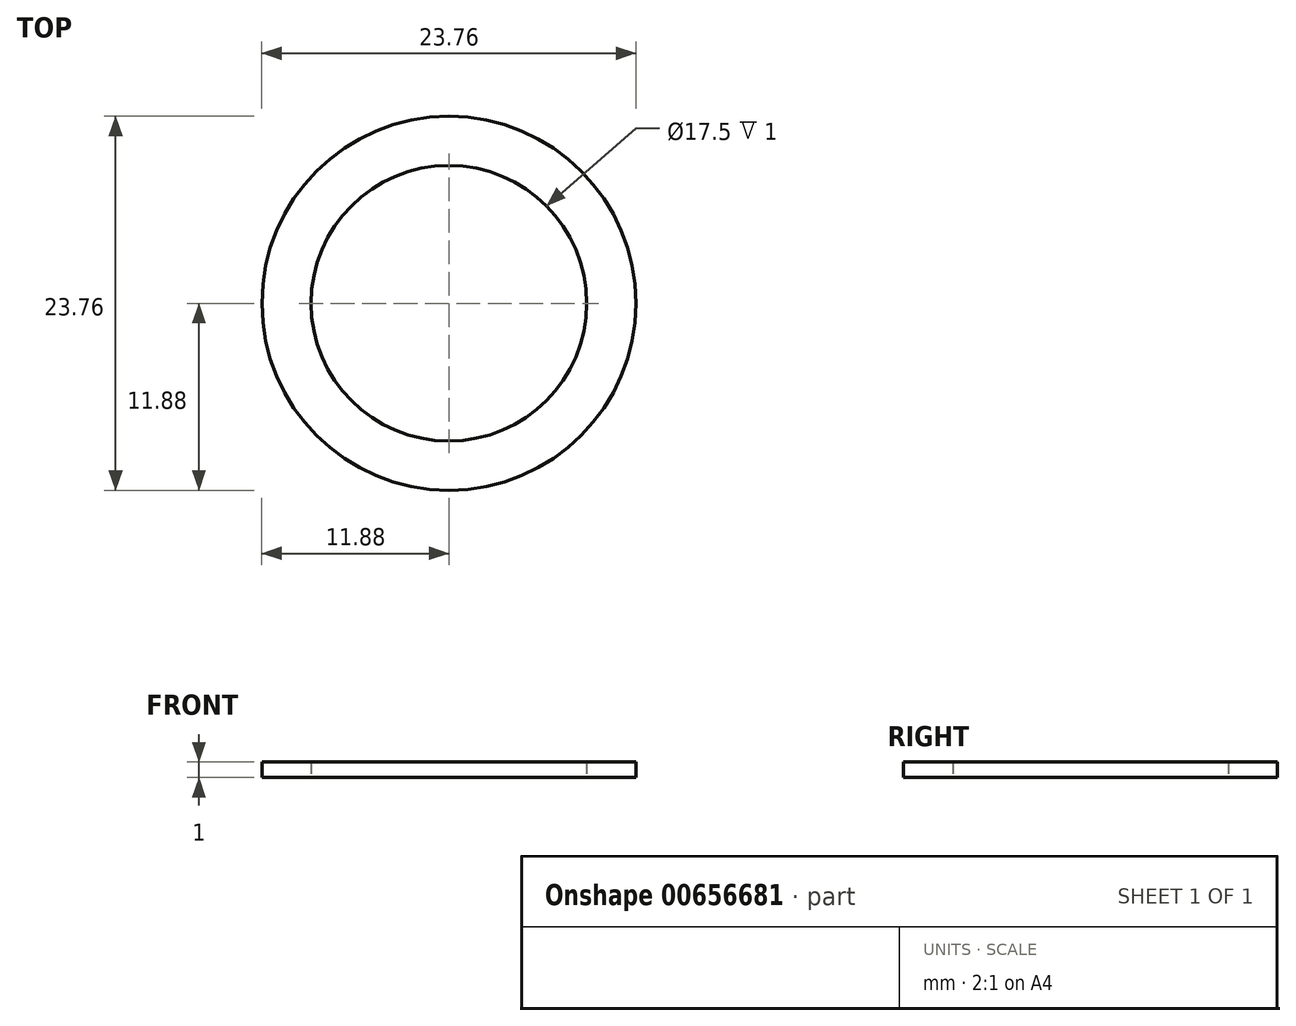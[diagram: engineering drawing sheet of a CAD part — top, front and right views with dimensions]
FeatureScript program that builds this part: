
annotation { "Feature Type Name" : "Feature", "Feature Type Description" : "" }
export const myFeature = defineFeature(function(context is Context, id is Id, definition is map)
    precondition{}
    {
        {
            var Q0;
            Q0=qCreatedBy(makeId("Top.planeOp"),FACE);
            var sketch = newSketch(context, id + "F0", { "sketchPlane" : qUnion([Q0])});
            skCircle(sketch, "E0", {"center": v(0, 0) * mm, "radius": 8.75 * mm});
            skCircle(sketch, "E1", {"center": v(0, 0) * mm, "radius": 11.88 * mm});
            skSolve(sketch);
        }
        {
            var Q0;
            Q0=makeQuery(id+"F0.imprint","IMPRINT",FACE,{"disambiguationData":[TD([[makeQuery(id+"F0.imprint","IMPRINT",EDGE,{"derivedFrom":sQuery(id+"F0.wireOp",EDGE,"E0")}),-1.0]])]});
            extrude(context, id + "F1", {"entities" : qUnion([Q0]), "endBound" : BoundingType.SYMMETRIC, "depth" : 1 * mm, "offsetDistance" : 25 * mm});
        }
    });
